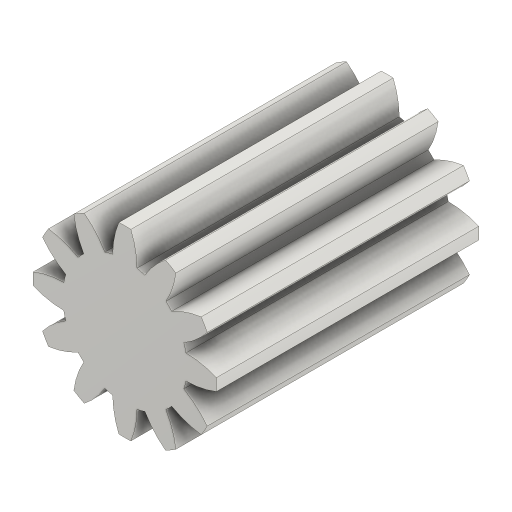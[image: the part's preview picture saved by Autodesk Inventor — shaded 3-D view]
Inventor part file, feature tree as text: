
AUTODESK INVENTOR PART (.ipt)
format: ipt  version: 2024 (Build 280153000, 153)  size: 345,600 bytes
history: native  units: mm (DEFAULTED — no unit token found)
features: plane x3, other x3, extrude x2, sketch x2, projected_geometry x1
ambient origin geometry x8: Origin, YZ Plane, XZ Plane, XY Plane, X Axis, Y Axis, Z Axis, Center Point
bodies: Solid1 (feature_tree)
feature tree (11):
  extrude  "Extrusion1"  Depth=20.0mm TaperAngle=0.0deg
  plane  "Work Plane2"
  plane  "Work Plane8"
  plane  "Work Plane9"
  other  "Spur Gear"
  extrude  "Extrusion2"  Depth=10.0mm TaperAngle=0.0deg
  sketch  "Sketch1"  dims[d0=28.0mm d1=20.0mm d2=0.0mm]
  other  "Srf1"
  sketch  "Sketch3"  dims[d3=24.0mm d4=10.0mm d5=0.0mm d16=60.0mm d17=0.0mm d34=15.0deg d39=0.0mm d41=0.0mm d43=60.0mm d46=60.0mm d47=0.0mm d48=0.0mm d49=20.0mm d50=0.0mm]
  projected_geometry  "Projected Loop1"
  other  "Pitch Diameter"
